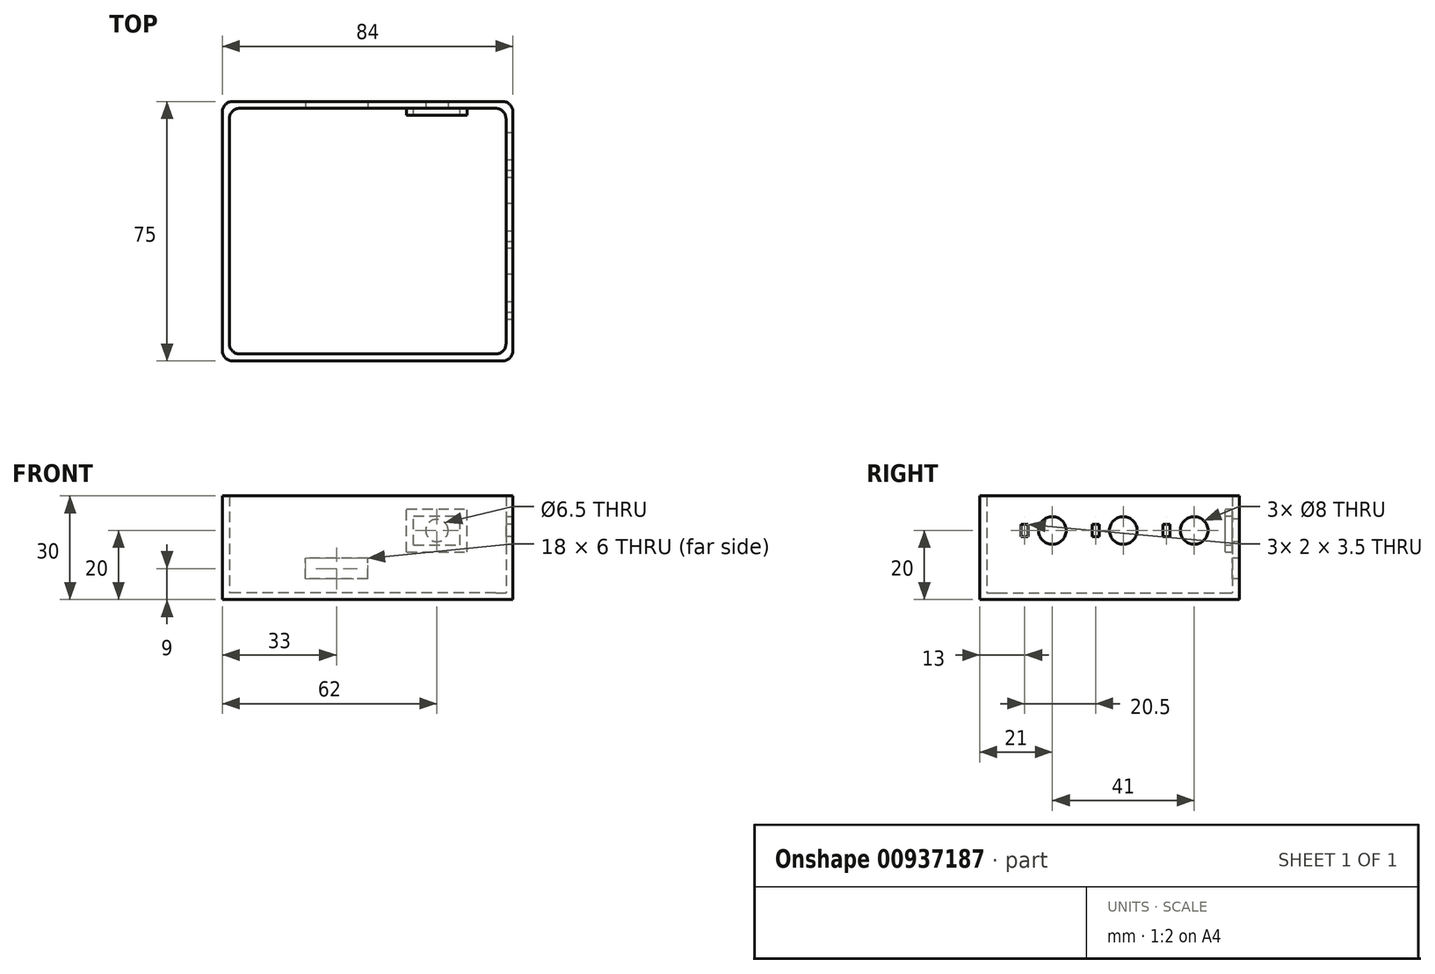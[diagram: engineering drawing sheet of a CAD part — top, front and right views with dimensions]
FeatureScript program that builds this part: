
annotation { "Feature Type Name" : "Feature", "Feature Type Description" : "" }
export const myFeature = defineFeature(function(context is Context, id is Id, definition is map)
    precondition{}
    {
        {
            var Q0;
            Q0=qCreatedBy(makeId("Top.planeOp"),FACE);
            var sketch = newSketch(context, id + "F0", { "sketchPlane" : qUnion([Q0])});
            skLineSegment(sketch, "E0.bottom", {"start": v(40, -35.5) * mm, "end": v(-40, -35.5) * mm});
            skLineSegment(sketch, "E0.top", {"start": v(40, 35.5) * mm, "end": v(-40, 35.5) * mm});
            skLineSegment(sketch, "E0.left", {"start": v(40, -35.5) * mm, "end": v(40, 35.5) * mm});
            skLineSegment(sketch, "E0.right", {"start": v(-40, -35.5) * mm, "end": v(-40, 35.5) * mm});
            skPoint(sketch, "E0.middle", {"position": v(0, 0) * mm});
            skLineSegment(sketch, "E1.0", {"start": v(-42, -37.5) * mm, "end": v(-42, 37.5) * mm});
            skLineSegment(sketch, "E1.1", {"start": v(42, -37.5) * mm, "end": v(-42, -37.5) * mm});
            skLineSegment(sketch, "E1.2", {"start": v(42, -37.5) * mm, "end": v(42, 37.5) * mm});
            skLineSegment(sketch, "E1.3", {"start": v(42, 37.5) * mm, "end": v(-42, 37.5) * mm});
            skSolve(sketch);
        }
        {
            var Q0;
            Q0=makeQuery(id+"F0.imprint","IMPRINT",FACE,{"disambiguationData":[TD([[makeQuery(id+"F0.imprint","IMPRINT",EDGE,{"derivedFrom":sQuery(id+"F0.wireOp",EDGE,"E0.bottom")}),-1.0]])]});
            extrude(context, id + "F1", {"entities" : qUnion([Q0]), "depth" : 2 * mm, "offsetDistance" : 25 * mm});
        }
        {
            var Q0;
            Q0=makeQuery(id+"F0.imprint","IMPRINT",FACE,{"disambiguationData":[TD([[makeQuery(id+"F0.imprint","IMPRINT",EDGE,{"derivedFrom":sQuery(id+"F0.wireOp",EDGE,"E0.bottom")}),1.0]])]});
            extrude(context, id + "F2", {"entities" : qUnion([Q0]), "operationType" : NewBodyOperationType.ADD, "depth" : 30 * mm, "offsetDistance" : 25 * mm});
        }
        {
            var Q0;
            Q0=makeQuery(id+"F2.opExtrude","SWEPT_FACE",FACE,{"disambiguationData":[OSD([sQuery(id+"F0.wireOp",EDGE,"E0.left")])]});
            var sketch = newSketch(context, id + "F3", { "sketchPlane" : qUnion([Q0])});
            skPoint(sketch, "E2", {"position": v(-35.5, 20) * mm});
            skLineSegment(sketch, "E3", {"start": v(-35.5, 20) * mm, "end": v(35.5, 20) * mm, "construction": true});
            skPoint(sketch, "E4", {"position": v(-24.5, 20) * mm});
            skCircle(sketch, "E5", {"center": v(-24.5, 20) * mm, "radius": 4 * mm});
            skPoint(sketch, "E6", {"position": v(-4, 20) * mm});
            skPoint(sketch, "E7", {"position": v(16.5, 20) * mm});
            skCircle(sketch, "E8", {"center": v(-4, 20) * mm, "radius": 4 * mm});
            skCircle(sketch, "E9", {"center": v(16.5, 20) * mm, "radius": 4 * mm});
            skPoint(sketch, "E10", {"position": v(-16.5, 20) * mm});
            skPoint(sketch, "E11", {"position": v(4, 20) * mm});
            skPoint(sketch, "E12", {"position": v(24.5, 20) * mm});
            skLineSegment(sketch, "E13.bottom", {"start": v(-15.5, 18.25) * mm, "end": v(-17.5, 18.25) * mm});
            skLineSegment(sketch, "E13.top", {"start": v(-15.5, 21.75) * mm, "end": v(-17.5, 21.75) * mm});
            skLineSegment(sketch, "E13.left", {"start": v(-15.5, 18.25) * mm, "end": v(-15.5, 21.75) * mm});
            skLineSegment(sketch, "E13.right", {"start": v(-17.5, 18.25) * mm, "end": v(-17.5, 21.75) * mm});
            skLineSegment(sketch, "E14.bottom", {"start": v(5, 18.25) * mm, "end": v(3, 18.25) * mm});
            skLineSegment(sketch, "E14.top", {"start": v(5, 21.75) * mm, "end": v(3, 21.75) * mm});
            skLineSegment(sketch, "E14.left", {"start": v(5, 18.25) * mm, "end": v(5, 21.75) * mm});
            skLineSegment(sketch, "E14.right", {"start": v(3, 18.25) * mm, "end": v(3, 21.75) * mm});
            skLineSegment(sketch, "E15.bottom", {"start": v(25.5, 18.25) * mm, "end": v(23.5, 18.25) * mm});
            skLineSegment(sketch, "E15.top", {"start": v(25.5, 21.75) * mm, "end": v(23.5, 21.75) * mm});
            skLineSegment(sketch, "E15.left", {"start": v(25.5, 18.25) * mm, "end": v(25.5, 21.75) * mm});
            skLineSegment(sketch, "E15.right", {"start": v(23.5, 18.25) * mm, "end": v(23.5, 21.75) * mm});
            skSolve(sketch);
        }
        {
            var Q0;
            Q0=makeQuery(id+"F3.imprint","IMPRINT",FACE,{"disambiguationData":[TD([[makeQuery(id+"F3.imprint","IMPRINT",EDGE,{"derivedFrom":sQuery(id+"F3.wireOp",EDGE,"E5")}),1.0]])]});
            var Q1;
            Q1=makeQuery(id+"F3.imprint","IMPRINT",FACE,{"disambiguationData":[TD([[makeQuery(id+"F3.imprint","IMPRINT",EDGE,{"derivedFrom":sQuery(id+"F3.wireOp",EDGE,"E8")}),1.0]])]});
            var Q2;
            Q2=makeQuery(id+"F3.imprint","IMPRINT",FACE,{"disambiguationData":[TD([[makeQuery(id+"F3.imprint","IMPRINT",EDGE,{"derivedFrom":sQuery(id+"F3.wireOp",EDGE,"E9")}),1.0]])]});
            extrude(context, id + "F4", {"entities" : qUnion([Q0, Q1, Q2]), "operationType" : NewBodyOperationType.REMOVE, "oppositeDirection" : true, "depth" : 25 * mm, "offsetDistance" : 25 * mm});
        }
        {
            var Q0;
            Q0=makeQuery(id+"F2.opExtrude","SWEPT_FACE",FACE,{"disambiguationData":[OSD([sQuery(id+"F0.wireOp",EDGE,"E0.top")])]});
            var sketch = newSketch(context, id + "F5", { "sketchPlane" : qUnion([Q0])});
            skPoint(sketch, "E16", {"position": v(0, 2) * mm});
            skPoint(sketch, "E17", {"position": v(0, 6) * mm});
            skLineSegment(sketch, "E18.bottom", {"start": v(0, 6) * mm, "end": v(-18, 6) * mm});
            skLineSegment(sketch, "E18.top", {"start": v(0, 12) * mm, "end": v(-18, 12) * mm});
            skLineSegment(sketch, "E18.left", {"start": v(0, 6) * mm, "end": v(0, 12) * mm});
            skLineSegment(sketch, "E18.right", {"start": v(-18, 6) * mm, "end": v(-18, 12) * mm});
            skPoint(sketch, "E19", {"position": v(20, 2) * mm});
            skPoint(sketch, "E20", {"position": v(20, 20) * mm});
            skCircle(sketch, "E21", {"center": v(20, 20) * mm, "radius": 3.25 * mm});
            skLineSegment(sketch, "E22.bottom", {"start": v(13.25, 15.75) * mm, "end": v(26.75, 15.75) * mm});
            skLineSegment(sketch, "E22.top", {"start": v(13.25, 24.25) * mm, "end": v(26.75, 24.25) * mm});
            skLineSegment(sketch, "E22.left", {"start": v(13.25, 15.75) * mm, "end": v(13.25, 24.25) * mm});
            skLineSegment(sketch, "E22.right", {"start": v(26.75, 15.75) * mm, "end": v(26.75, 24.25) * mm});
            skLineSegment(sketch, "E23.0", {"start": v(11.25, 13.75) * mm, "end": v(11.25, 26.25) * mm});
            skLineSegment(sketch, "E23.1", {"start": v(11.25, 13.75) * mm, "end": v(28.75, 13.75) * mm});
            skLineSegment(sketch, "E23.2", {"start": v(28.75, 13.75) * mm, "end": v(28.75, 26.25) * mm});
            skLineSegment(sketch, "E23.3", {"start": v(11.25, 26.25) * mm, "end": v(28.75, 26.25) * mm});
            skSolve(sketch);
        }
        {
            var Q0;
            Q0=makeQuery(id+"F5.imprint","IMPRINT",FACE,{"disambiguationData":[TD([[makeQuery(id+"F5.imprint","IMPRINT",EDGE,{"derivedFrom":sQuery(id+"F5.wireOp",EDGE,"E18.bottom")}),-1.0]])]});
            extrude(context, id + "F6", {"entities" : qUnion([Q0]), "operationType" : NewBodyOperationType.REMOVE, "oppositeDirection" : true, "depth" : 25 * mm, "offsetDistance" : 25 * mm});
        }
        {
            var Q0;
            Q0=makeQuery(id+"F5.imprint","IMPRINT",FACE,{"disambiguationData":[TD([[makeQuery(id+"F5.imprint","IMPRINT",EDGE,{"derivedFrom":sQuery(id+"F5.wireOp",EDGE,"E22.bottom")}),-1.0]])]});
            extrude(context, id + "F7", {"entities" : qUnion([Q0]), "operationType" : NewBodyOperationType.ADD, "depth" : 2 * mm, "offsetDistance" : 25 * mm});
        }
        {
            var Q0;
            Q0=makeQuery(id+"F5.imprint","IMPRINT",FACE,{"disambiguationData":[TD([[makeQuery(id+"F5.imprint","IMPRINT",EDGE,{"derivedFrom":sQuery(id+"F5.wireOp",EDGE,"E21")}),1.0]])]});
            extrude(context, id + "F8", {"entities" : qUnion([Q0]), "operationType" : NewBodyOperationType.REMOVE, "oppositeDirection" : true, "depth" : 25 * mm, "offsetDistance" : 25 * mm});
        }
        {
            var Q0;
            Q0=makeQuery(id+"F3.imprint","IMPRINT",FACE,{"disambiguationData":[TD([[makeQuery(id+"F3.imprint","IMPRINT",EDGE,{"derivedFrom":sQuery(id+"F3.wireOp",EDGE,"E13.bottom")}),-1.0]])]});
            var Q1;
            Q1=makeQuery(id+"F3.imprint","IMPRINT",FACE,{"disambiguationData":[TD([[makeQuery(id+"F3.imprint","IMPRINT",EDGE,{"derivedFrom":sQuery(id+"F3.wireOp",EDGE,"E14.bottom")}),-1.0]])]});
            var Q2;
            Q2=makeQuery(id+"F3.imprint","IMPRINT",FACE,{"disambiguationData":[TD([[makeQuery(id+"F3.imprint","IMPRINT",EDGE,{"derivedFrom":sQuery(id+"F3.wireOp",EDGE,"E15.bottom")}),-1.0]])]});
            extrude(context, id + "F9", {"entities" : qUnion([Q0, Q1, Q2]), "operationType" : NewBodyOperationType.REMOVE, "oppositeDirection" : true, "depth" : 25 * mm, "offsetDistance" : 25 * mm});
        }
        {
            var Q0;
            Q0=makeQuery(id+"F2.opExtrude","SWEPT_EDGE",EDGE,{"disambiguationData":[OSD([sQuery(id+"F0.wireOp",EDGE,"E0.top"),sQuery(id+"F0.wireOp",EDGE,"E0.left")])]});
            var Q1;
            Q1=makeQuery(id+"F2.opExtrude","SWEPT_EDGE",EDGE,{"disambiguationData":[OSD([sQuery(id+"F0.wireOp",EDGE,"E0.top"),sQuery(id+"F0.wireOp",EDGE,"E0.right")])]});
            var Q2;
            Q2=makeQuery(id+"F2.opExtrude","SWEPT_EDGE",EDGE,{"disambiguationData":[OSD([sQuery(id+"F0.wireOp",EDGE,"E0.bottom"),sQuery(id+"F0.wireOp",EDGE,"E0.right")])]});
            var Q3;
            Q3=makeQuery(id+"F2.opExtrude","SWEPT_EDGE",EDGE,{"disambiguationData":[OSD([sQuery(id+"F0.wireOp",EDGE,"E0.bottom"),sQuery(id+"F0.wireOp",EDGE,"E0.left")])]});
            fillet(context, id + "F10", {"entities" : qUnion([Q0, Q1, Q2, Q3]), "radius" : 3 * mm, "tangentPropagation" : true, "allowEdgeOverflow" : false});
        }
        {
            var Q0;
            Q0=makeQuery(id+"F2.opExtrude","SWEPT_EDGE",EDGE,{"disambiguationData":[OSD([sQuery(id+"F0.wireOp",EDGE,"E1.1"),sQuery(id+"F0.wireOp",EDGE,"E1.2")])]});
            var Q1;
            Q1=makeQuery(id+"F2.opExtrude","SWEPT_EDGE",EDGE,{"disambiguationData":[OSD([sQuery(id+"F0.wireOp",EDGE,"E1.2"),sQuery(id+"F0.wireOp",EDGE,"E1.3")])]});
            var Q2;
            Q2=makeQuery(id+"F2.opExtrude","SWEPT_EDGE",EDGE,{"disambiguationData":[OSD([sQuery(id+"F0.wireOp",EDGE,"E1.0"),sQuery(id+"F0.wireOp",EDGE,"E1.1")])]});
            var Q3;
            Q3=makeQuery(id+"F2.opExtrude","SWEPT_EDGE",EDGE,{"disambiguationData":[OSD([sQuery(id+"F0.wireOp",EDGE,"E1.0"),sQuery(id+"F0.wireOp",EDGE,"E1.3")])]});
            fillet(context, id + "F11", {"entities" : qUnion([Q0, Q1, Q2, Q3]), "radius" : 3 * mm, "tangentPropagation" : true, "allowEdgeOverflow" : false});
        }
    });
